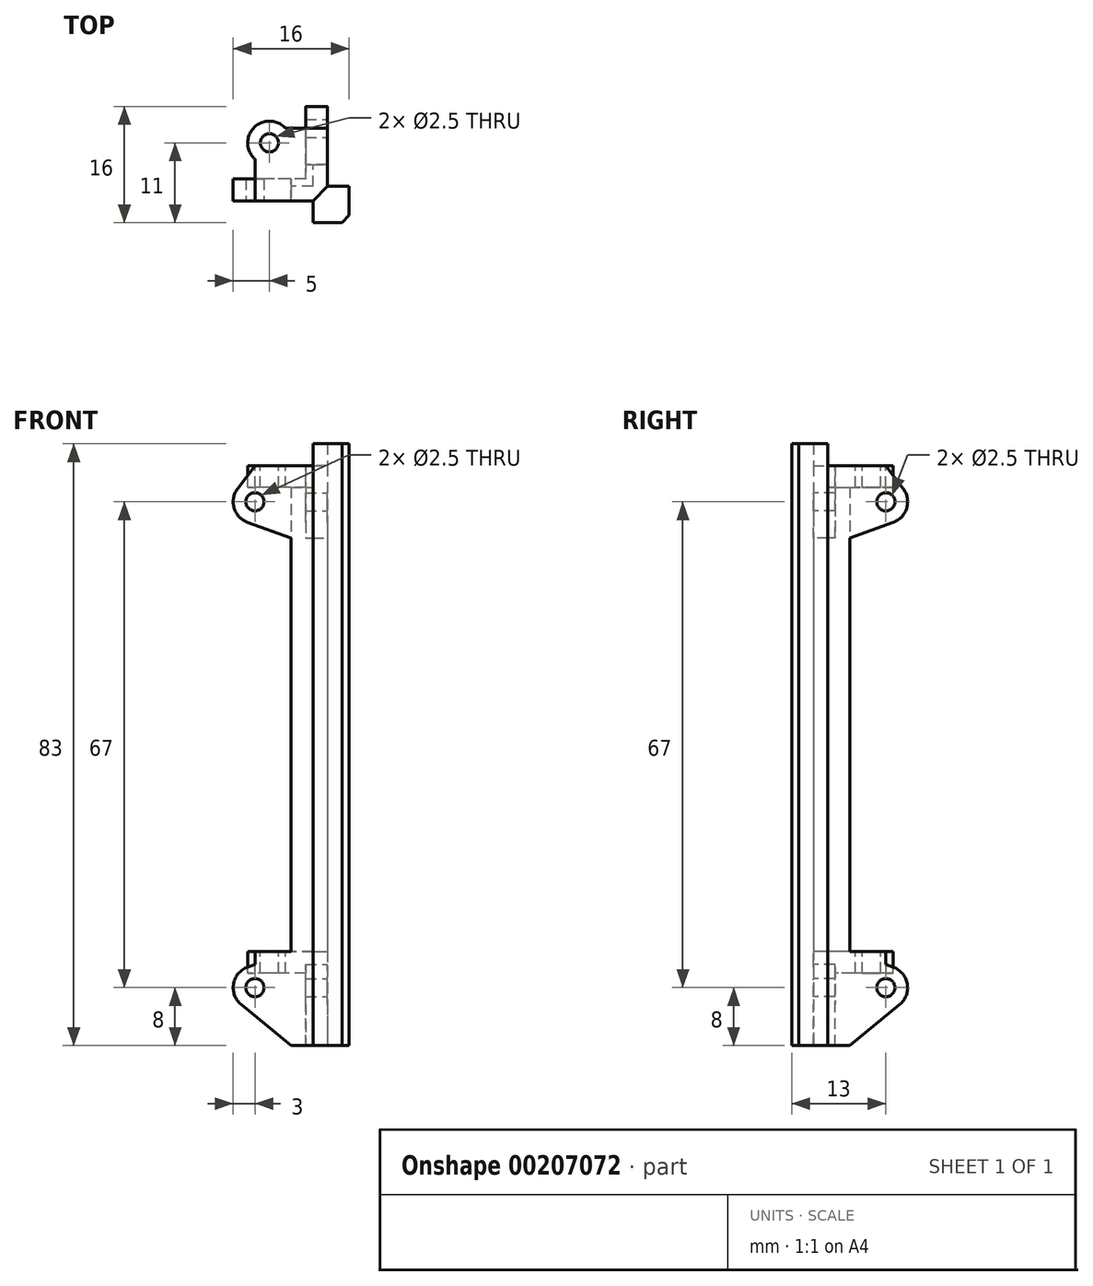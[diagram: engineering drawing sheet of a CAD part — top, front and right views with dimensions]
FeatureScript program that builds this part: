
annotation { "Feature Type Name" : "Feature", "Feature Type Description" : "" }
export const myFeature = defineFeature(function(context is Context, id is Id, definition is map)
    precondition{}
    {
        {
            var Q0;
            Q0=qCreatedBy(makeId("Top.planeOp"),FACE);
            var sketch = newSketch(context, id + "F0", { "sketchPlane" : qUnion([Q0])});
            skLineSegment(sketch, "E0", {"start": v(0, 0) * mm, "end": v(40, 0) * mm, "construction": true});
            skLineSegment(sketch, "E1", {"start": v(40, 0) * mm, "end": v(45, 0) * mm});
            skLineSegment(sketch, "E2", {"start": v(45, 0) * mm, "end": v(45, 5) * mm});
            skLineSegment(sketch, "E3", {"start": v(40, 0) * mm, "end": v(40, 3) * mm});
            skLineSegment(sketch, "E4", {"start": v(45, 5) * mm, "end": v(42, 5) * mm});
            skLineSegment(sketch, "E5", {"start": v(40, 3) * mm, "end": v(37, 3) * mm});
            skLineSegment(sketch, "E6", {"start": v(42, 5) * mm, "end": v(42, 8) * mm});
            skLineSegment(sketch, "E7", {"start": v(37, 3) * mm, "end": v(37, 5) * mm});
            skLineSegment(sketch, "E8", {"start": v(42, 8) * mm, "end": v(40, 8) * mm});
            skLineSegment(sketch, "E9", {"start": v(37, 5) * mm, "end": v(40, 5) * mm});
            skLineSegment(sketch, "E10", {"start": v(40, 5) * mm, "end": v(40, 8) * mm});
            skSolve(sketch);
        }
        {
            var Q0;
            Q0 = qSketchRegion(id + "F0", true);
            extrude(context, id + "F1", {"entities" : qUnion([Q0]), "depth" : 80 * mm});
        }
        {
            var Q0;
            Q0=makeQuery(id+"F1.opExtrude","CAP_FACE",FACE,{"disambiguationData":[OSD([sQuery(id+"F0.wireOp",EDGE,"E1"),sQuery(id+"F0.wireOp",EDGE,"E2"),sQuery(id+"F0.wireOp",EDGE,"E3"),sQuery(id+"F0.wireOp",EDGE,"E4"),sQuery(id+"F0.wireOp",EDGE,"E5"),sQuery(id+"F0.wireOp",EDGE,"E6"),sQuery(id+"F0.wireOp",EDGE,"E7"),sQuery(id+"F0.wireOp",EDGE,"E8"),sQuery(id+"F0.wireOp",EDGE,"E9"),sQuery(id+"F0.wireOp",EDGE,"E10")])],"isStart":false});
            var sketch = newSketch(context, id + "F2", { "sketchPlane" : qUnion([Q0])});
            skLineSegment(sketch, "E11", {"start": v(40, 3) * mm, "end": v(42, 5) * mm});
            skLineSegment(sketch, "E12", {"start": v(37, 3) * mm, "end": v(34, 3) * mm, "construction": true});
            skLineSegment(sketch, "E13", {"start": v(34, 3) * mm, "end": v(34, 11) * mm, "construction": true});
            skCircle(sketch, "E14", {"center": v(34, 11) * mm, "radius": 1.25 * mm});
            skCircle(sketch, "E15", {"center": v(34, 11) * mm, "radius": 3 * mm});
            skLineSegment(sketch, "E16", {"start": v(37, 3) * mm, "end": v(40, 3) * mm});
            skLineSegment(sketch, "E17", {"start": v(42, 5) * mm, "end": v(42, 8) * mm});
            skLineSegment(sketch, "E18", {"start": v(40, 3) * mm, "end": v(40, 0) * mm});
            skLineSegment(sketch, "E19", {"start": v(40, 0) * mm, "end": v(45, 0) * mm});
            skLineSegment(sketch, "E20", {"start": v(45, 0) * mm, "end": v(45, 5) * mm});
            skLineSegment(sketch, "E21", {"start": v(45, 5) * mm, "end": v(42, 5) * mm});
            skLineSegment(sketch, "E22", {"start": v(37, 3) * mm, "end": v(32, 3) * mm});
            skLineSegment(sketch, "E23", {"start": v(32, 3) * mm, "end": v(32, 8.76) * mm});
            skLineSegment(sketch, "E24", {"start": v(42, 8) * mm, "end": v(42, 13) * mm});
            skLineSegment(sketch, "E25", {"start": v(42, 13) * mm, "end": v(36.24, 13) * mm});
            skSolve(sketch);
        }
        {
            var Q0;
            Q0=makeQuery(id+"F2.imprint","IMPRINT",FACE,{"disambiguationData":[TD([[makeQuery(id+"F2.imprint","IMPRINT",EDGE,{"derivedFrom":sQuery(id+"F2.wireOp",EDGE,"E22")}),-1.0]])]});
            var Q1;
            Q1=makeQuery(id+"F2.imprint","IMPRINT",FACE,{"disambiguationData":[TD([[makeQuery(id+"F2.imprint","IMPRINT",EDGE,{"derivedFrom":sQuery(id+"F2.wireOp",EDGE,"E14")}),-1.0]])]});
            extrude(context, id + "F3", {"entities" : qUnion([Q0, Q1]), "operationType" : NewBodyOperationType.ADD, "oppositeDirection" : true, "depth" : 3 * mm});
        }
        {
            var Q0;
            Q0=makeQuery(id+"F2.imprint","IMPRINT",FACE,{"disambiguationData":[TD([[makeQuery(id+"F2.imprint","IMPRINT",EDGE,{"derivedFrom":sQuery(id+"F2.wireOp",EDGE,"E11")}),-1.0]])]});
            extrude(context, id + "F4", {"entities" : qUnion([Q0]), "operationType" : NewBodyOperationType.ADD, "depth" : 3 * mm});
        }
        {
            var Q0;
            Q0=makeQuery(id+"F1.opExtrude","SWEPT_FACE",FACE,{"disambiguationData":[OSD([sQuery(id+"F0.wireOp",EDGE,"E5")])]});
            var sketch = newSketch(context, id + "F5", { "sketchPlane" : qUnion([Q0])});
            skLineSegment(sketch, "E26", {"start": v(40, 75) * mm, "end": v(32, 75) * mm, "construction": true});
            skCircle(sketch, "E27", {"center": v(32, 75) * mm, "radius": 1.25 * mm});
            skCircle(sketch, "E28", {"center": v(32, 75) * mm, "radius": 3 * mm});
            skLineSegment(sketch, "E29", {"start": v(37, 69.99) * mm, "end": v(30.97, 72.18) * mm});
            skLineSegment(sketch, "E30", {"start": v(32, 75) * mm, "end": v(32, 78) * mm, "construction": true});
            skLineSegment(sketch, "E31", {"start": v(32, 78) * mm, "end": v(32, 80) * mm});
            skLineSegment(sketch, "E32", {"start": v(32, 80) * mm, "end": v(29.6, 76.8) * mm});
            skSolve(sketch);
        }
        {
            var Q0;
            Q0=makeQuery(id+"F5.imprint","IMPRINT",FACE,{"disambiguationData":[TD([[makeQuery(id+"F5.imprint","IMPRINT",EDGE,{"derivedFrom":sQuery(id+"F5.wireOp",EDGE,"E27")}),-1.0]])]});
            var Q1;
            {var subQ0=sQuery(id+"F5.wireOp",EDGE,"E31");Q1=makeQuery(id+"F5.imprint","IMPRINT",FACE,{"disambiguationData":[TD([[makeQuery(id+"F5.imprint","IMPRINT",EDGE,{"derivedFrom":subQ0}),1.0]])]});}
            var Q2;
            {var subQ4=sQuery(id+"F5.wireOp",EDGE,"E29");Q2=makeQuery(id+"F5.imprint","IMPRINT",FACE,{"disambiguationData":[TD([[makeQuery(id+"F5.imprint","IMPRINT",EDGE,{"derivedFrom":subQ4}),-1.0]])]});}
            extrude(context, id + "F6", {"entities" : qUnion([Q0, Q1, Q2]), "operationType" : NewBodyOperationType.ADD, "oppositeDirection" : true, "depth" : 3 * mm});
        }
        {
            var Q0;
            Q0=makeQuery(id+"F3.boolean.opBoolean","MERGE",FACE,{"derivedFrom":[makeQuery(id+"F1.opExtrude","SWEPT_FACE",FACE,{"disambiguationData":[OSD([sQuery(id+"F0.wireOp",EDGE,"E6")])]}),makeQuery(id+"F3.opExtrude","SWEPT_FACE",FACE,{"disambiguationData":[OSD([sQuery(id+"F2.wireOp",EDGE,"E24")])]})]});
            var sketch = newSketch(context, id + "F7", { "sketchPlane" : qUnion([Q0])});
            skLineSegment(sketch, "E33", {"start": v(5, 75) * mm, "end": v(13, 75) * mm, "construction": true});
            skCircle(sketch, "E34", {"center": v(13, 75) * mm, "radius": 1.25 * mm});
            skCircle(sketch, "E35", {"center": v(13, 75) * mm, "radius": 3 * mm});
            skLineSegment(sketch, "E36", {"start": v(13, 80) * mm, "end": v(15.4, 76.8) * mm});
            skLineSegment(sketch, "E37", {"start": v(14.03, 72.18) * mm, "end": v(8, 69.99) * mm});
            skSolve(sketch);
        }
        {
            var Q0;
            {var subQ0=sQuery(id+"F7.wireOp",EDGE,"E37");Q0=makeQuery(id+"F7.imprint","IMPRINT",FACE,{"disambiguationData":[TD([[makeQuery(id+"F7.imprint","IMPRINT",EDGE,{"derivedFrom":subQ0}),-1.0]])]});}
            var Q1;
            Q1=makeQuery(id+"F7.imprint","IMPRINT",FACE,{"disambiguationData":[TD([[makeQuery(id+"F7.imprint","IMPRINT",EDGE,{"derivedFrom":sQuery(id+"F7.wireOp",EDGE,"E34")}),-1.0]])]});
            var Q2;
            {var subQ0=sQuery(id+"F7.wireOp",EDGE,"E36");Q2=makeQuery(id+"F7.imprint","IMPRINT",FACE,{"disambiguationData":[TD([[makeQuery(id+"F7.imprint","IMPRINT",EDGE,{"derivedFrom":subQ0}),-1.0]])]});}
            extrude(context, id + "F8", {"entities" : qUnion([Q0, Q1, Q2]), "operationType" : NewBodyOperationType.ADD, "oppositeDirection" : true, "depth" : 3 * mm});
        }
        {
            var Q0;
            Q0=makeQuery(id+"F4.boolean.opBoolean","MERGE",EDGE,{"derivedFrom":[makeQuery(id+"F1.opExtrude","SWEPT_EDGE",EDGE,{"disambiguationData":[OSD([sQuery(id+"F0.wireOp",EDGE,"E1"),sQuery(id+"F0.wireOp",EDGE,"E2")])]}),makeQuery(id+"F4.opExtrude","SWEPT_EDGE",EDGE,{"disambiguationData":[OSD([sQuery(id+"F2.wireOp",EDGE,"E19"),sQuery(id+"F2.wireOp",EDGE,"E20")])]})]});
            chamfer(context, id + "F9", {"entities" : qUnion([Q0]), "width" : 1 * mm, "tangentPropagation" : true});
        }
        {
            var Q0;
            {var subQ0=sQuery(id+"F2.wireOp",EDGE,"E22");var subQ1=sQuery(id+"F0.wireOp",EDGE,"E5");Q0=makeQuery(id+"F6.boolean.opBoolean","MERGE",FACE,{"derivedFrom":[makeQuery(id+"F3.boolean.opBoolean","MERGE",FACE,{"derivedFrom":[makeQuery(id+"F1.opExtrude","SWEPT_FACE",FACE,{"disambiguationData":[OSD([subQ1])]}),makeQuery(id+"F3.opExtrude","SWEPT_FACE",FACE,{"disambiguationData":[OSD([subQ0])]})]}),makeQuery(id+"F6.opExtrude","CAP_FACE",FACE,{"disambiguationData":[OSD([subQ1,sQuery(id+"F0.wireOp",EDGE,"E7"),subQ0,sQuery(id+"F2.wireOp",EDGE,"E23"),sQuery(id+"F5.wireOp",EDGE,"E27"),sQuery(id+"F5.wireOp",EDGE,"E28"),sQuery(id+"F5.wireOp",EDGE,"E29"),sQuery(id+"F5.wireOp",EDGE,"E31"),sQuery(id+"F5.wireOp",EDGE,"E32")])],"isStart":true})]});}
            var sketch = newSketch(context, id + "F10", { "sketchPlane" : qUnion([Q0])});
            skLineSegment(sketch, "E38", {"start": v(40, 8) * mm, "end": v(32, 8) * mm, "construction": true});
            skCircle(sketch, "E39", {"center": v(32, 8) * mm, "radius": 1.25 * mm});
            skCircle(sketch, "E40", {"center": v(32, 8) * mm, "radius": 3 * mm});
            skLineSegment(sketch, "E41", {"start": v(37, 0) * mm, "end": v(30.1, 5.68) * mm});
            skLineSegment(sketch, "E42", {"start": v(30.98, 10.82) * mm, "end": v(37, 13) * mm});
            skLineSegment(sketch, "E43", {"start": v(37, 13) * mm, "end": v(37, 0) * mm});
            skLineSegment(sketch, "E44", {"start": v(37, 13) * mm, "end": v(40, 13) * mm});
            skLineSegment(sketch, "E45", {"start": v(37, 0) * mm, "end": v(40, 0) * mm});
            skLineSegment(sketch, "E46", {"start": v(40, 0) * mm, "end": v(40, 13) * mm});
            skSolve(sketch);
        }
        {
            var Q0;
            Q0=makeQuery(id+"F10.imprint","IMPRINT",FACE,{"disambiguationData":[TD([[makeQuery(id+"F10.imprint","IMPRINT",EDGE,{"derivedFrom":sQuery(id+"F10.wireOp",EDGE,"E39")}),-1.0]])]});
            var Q1;
            {var subQ0=sQuery(id+"F10.wireOp",EDGE,"E41");Q1=makeQuery(id+"F10.imprint","IMPRINT",FACE,{"disambiguationData":[TD([[makeQuery(id+"F10.imprint","IMPRINT",EDGE,{"derivedFrom":subQ0}),-1.0]])]});}
            var Q2;
            Q2=makeQuery(id+"F10.imprint","IMPRINT",FACE,{"disambiguationData":[TD([[makeQuery(id+"F10.imprint","IMPRINT",EDGE,{"derivedFrom":sQuery(id+"F10.wireOp",EDGE,"E43")}),1.0]])]});
            extrude(context, id + "F11", {"entities" : qUnion([Q0, Q1, Q2]), "operationType" : NewBodyOperationType.ADD, "oppositeDirection" : true, "depth" : 3 * mm});
        }
        {
            var Q0;
            {var subQ0=sQuery(id+"F2.wireOp",EDGE,"E24");var subQ1=sQuery(id+"F0.wireOp",EDGE,"E6");Q0=makeQuery(id+"F8.boolean.opBoolean","MERGE",FACE,{"derivedFrom":[makeQuery(id+"F3.boolean.opBoolean","MERGE",FACE,{"derivedFrom":[makeQuery(id+"F1.opExtrude","SWEPT_FACE",FACE,{"disambiguationData":[OSD([subQ1])]}),makeQuery(id+"F3.opExtrude","SWEPT_FACE",FACE,{"disambiguationData":[OSD([subQ0])]})]}),makeQuery(id+"F8.opExtrude","CAP_FACE",FACE,{"disambiguationData":[OSD([subQ1,sQuery(id+"F0.wireOp",EDGE,"E8"),subQ0,sQuery(id+"F2.wireOp",EDGE,"E25"),sQuery(id+"F7.wireOp",EDGE,"E34"),sQuery(id+"F7.wireOp",EDGE,"E35"),sQuery(id+"F7.wireOp",EDGE,"E36"),sQuery(id+"F7.wireOp",EDGE,"E37")])],"isStart":true})]});}
            var sketch = newSketch(context, id + "F12", { "sketchPlane" : qUnion([Q0])});
            skLineSegment(sketch, "E47", {"start": v(5, 8) * mm, "end": v(13, 8) * mm, "construction": true});
            skCircle(sketch, "E48", {"center": v(13, 8) * mm, "radius": 3 * mm});
            skCircle(sketch, "E49", {"center": v(13, 8) * mm, "radius": 1.25 * mm});
            skLineSegment(sketch, "E50", {"start": v(14.02, 10.82) * mm, "end": v(8, 13) * mm});
            skLineSegment(sketch, "E51", {"start": v(8, 13) * mm, "end": v(5, 13) * mm});
            skLineSegment(sketch, "E52", {"start": v(14.9, 5.68) * mm, "end": v(8, 0) * mm});
            skLineSegment(sketch, "E53", {"start": v(8, 0) * mm, "end": v(5, 0) * mm});
            skLineSegment(sketch, "E54", {"start": v(5, 0) * mm, "end": v(5, 13) * mm});
            skSolve(sketch);
        }
        {
            var Q0;
            {var subQ0=sQuery(id+"F12.wireOp",EDGE,"E51");Q0=makeQuery(id+"F12.imprint","IMPRINT",FACE,{"disambiguationData":[TD([[makeQuery(id+"F12.imprint","IMPRINT",EDGE,{"derivedFrom":subQ0}),1.0]])]});}
            var Q1;
            {var subQ0=sQuery(id+"F12.wireOp",EDGE,"E50");Q1=makeQuery(id+"F12.imprint","IMPRINT",FACE,{"disambiguationData":[TD([[makeQuery(id+"F12.imprint","IMPRINT",EDGE,{"derivedFrom":subQ0}),1.0]])]});}
            var Q2;
            Q2=makeQuery(id+"F12.imprint","IMPRINT",FACE,{"disambiguationData":[TD([[makeQuery(id+"F12.imprint","IMPRINT",EDGE,{"derivedFrom":sQuery(id+"F12.wireOp",EDGE,"E49")}),-1.0]])]});
            extrude(context, id + "F13", {"entities" : qUnion([Q0, Q1, Q2]), "operationType" : NewBodyOperationType.ADD, "oppositeDirection" : true, "depth" : 3 * mm});
        }
        {
            var Q0;
            {var subQ0=sQuery(id+"F2.wireOp",EDGE,"E22");var subQ1=sQuery(id+"F0.wireOp",EDGE,"E5");Q0=makeQuery(id+"F11.boolean.opBoolean","MERGE",FACE,{"derivedFrom":[makeQuery(id+"F6.boolean.opBoolean","MERGE",FACE,{"derivedFrom":[makeQuery(id+"F3.boolean.opBoolean","MERGE",FACE,{"derivedFrom":[makeQuery(id+"F1.opExtrude","SWEPT_FACE",FACE,{"disambiguationData":[OSD([subQ1])]}),makeQuery(id+"F3.opExtrude","SWEPT_FACE",FACE,{"disambiguationData":[OSD([subQ0])]})]}),makeQuery(id+"F6.opExtrude","CAP_FACE",FACE,{"disambiguationData":[OSD([subQ1,sQuery(id+"F0.wireOp",EDGE,"E7"),subQ0,sQuery(id+"F2.wireOp",EDGE,"E23"),sQuery(id+"F5.wireOp",EDGE,"E27"),sQuery(id+"F5.wireOp",EDGE,"E28"),sQuery(id+"F5.wireOp",EDGE,"E29"),sQuery(id+"F5.wireOp",EDGE,"E31"),sQuery(id+"F5.wireOp",EDGE,"E32")])],"isStart":true})]}),makeQuery(id+"F11.opExtrude","CAP_FACE",FACE,{"disambiguationData":[OSD([sQuery(id+"F10.wireOp",EDGE,"E39"),sQuery(id+"F10.wireOp",EDGE,"E40"),sQuery(id+"F10.wireOp",EDGE,"E41"),sQuery(id+"F10.wireOp",EDGE,"E42"),sQuery(id+"F10.wireOp",EDGE,"E44"),sQuery(id+"F10.wireOp",EDGE,"E45"),sQuery(id+"F10.wireOp",EDGE,"E46")])],"isStart":true})]});}
            var sketch = newSketch(context, id + "F14", { "sketchPlane" : qUnion([Q0])});
            skLineSegment(sketch, "E55", {"start": v(40, 10) * mm, "end": v(32, 10) * mm});
            skLineSegment(sketch, "E56", {"start": v(32, 10) * mm, "end": v(32, 13) * mm});
            skLineSegment(sketch, "E57", {"start": v(32, 13) * mm, "end": v(40, 13) * mm});
            skLineSegment(sketch, "E58", {"start": v(40, 13) * mm, "end": v(40, 10) * mm});
            skLineSegment(sketch, "E59", {"start": v(40, 13) * mm, "end": v(42, 13) * mm});
            skLineSegment(sketch, "E60", {"start": v(42, 13) * mm, "end": v(42, 10) * mm});
            skLineSegment(sketch, "E61", {"start": v(42, 10) * mm, "end": v(40, 10) * mm});
            skSolve(sketch);
        }
        {
            var Q0;
            Q0 = qSketchRegion(id + "F14", true);
            extrude(context, id + "F15", {"entities" : qUnion([Q0]), "operationType" : NewBodyOperationType.ADD, "oppositeDirection" : true, "depth" : 10 * mm});
        }
        {
            var Q0;
            Q0=makeQuery(id+"F15.boolean.opBoolean","MERGE",FACE,{"derivedFrom":[makeQuery(id+"F11.opExtrude","SWEPT_FACE",FACE,{"disambiguationData":[OSD([sQuery(id+"F10.wireOp",EDGE,"E44")])]}),makeQuery(id+"F15.opExtrude","SWEPT_FACE",FACE,{"disambiguationData":[OSD([sQuery(id+"F14.wireOp",EDGE,"E57"),sQuery(id+"F14.wireOp",EDGE,"E59")])]})]});
            var sketch = newSketch(context, id + "F16", { "sketchPlane" : qUnion([Q0])});
            skLineSegment(sketch, "E62", {"start": v(40, 5) * mm, "end": v(40, 11) * mm, "construction": true});
            skLineSegment(sketch, "E63", {"start": v(40, 11) * mm, "end": v(34, 11) * mm, "construction": true});
            skCircle(sketch, "E64", {"center": v(34, 11) * mm, "radius": 1.25 * mm});
            skCircle(sketch, "E65", {"center": v(34, 11) * mm, "radius": 3 * mm});
            skSolve(sketch);
        }
        {
            var Q0;
            {var subQ0=sQuery(id+"F16.wireOp",EDGE,"E65");var subQ1=sQuery(id+"F14.wireOp",EDGE,"E57");var subQ2=makeQuery(id+"F15.opExtrude","SWEPT_EDGE",EDGE,{"disambiguationData":[OSD([sQuery(id+"F14.wireOp",EDGE,"E56"),subQ1])]});var subQ3=makeQuery(id+"F16.imprint","INTERSECT",VERTEX,{"derivedFrom":[subQ2,subQ0]});Q0=makeQuery(id+"F16.imprint","IMPRINT",FACE,{"disambiguationData":[TD([[makeQuery(id+"F16.imprint","IMPRINT",EDGE,{"disambiguationData":[TD([[subQ3,1.0]])],"derivedFrom":subQ0}),1.0]])]});}
            extrude(context, id + "F17", {"entities" : qUnion([Q0]), "operationType" : NewBodyOperationType.ADD, "oppositeDirection" : true, "depth" : 3 * mm});
        }
        {
            var Q0;
            Q0=makeQuery(id+"F16.imprint","IMPRINT",FACE,{"disambiguationData":[TD([[makeQuery(id+"F16.imprint","IMPRINT",EDGE,{"derivedFrom":sQuery(id+"F16.wireOp",EDGE,"E64")}),1.0]])]});
            extrude(context, id + "F18", {"entities" : qUnion([Q0]), "operationType" : NewBodyOperationType.REMOVE, "oppositeDirection" : true, "depth" : 25 * mm});
        }
    });
